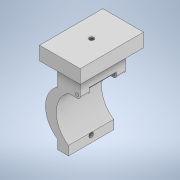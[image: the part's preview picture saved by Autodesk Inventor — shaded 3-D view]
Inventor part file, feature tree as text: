
AUTODESK INVENTOR PART (.ipt)
format: ipt  version: 2021 (Build 250183000, 183)  size: 187,904 bytes
history: native  units: in
note: dims shown in document units (in); Inventor stores cm internally (conversion verified against a paired STEP export)
features: sketch x6, extrude x5, hole x2, fillet x1
ambient origin geometry x8: Origin, YZ Plane, XZ Plane, XY Plane, X Axis, Y Axis, Z Axis, Center Point
bodies: Solid1 (feature_tree)
feature tree (14):
  extrude  "Extrusion1"  Depth=3.937in TaperAngle=0.0deg
  extrude  "Extrusion6"  Depth=1.9685in
  extrude  "Extrusion7"  Depth=0.7874in
  hole  "Hole3"  [1 undecoded]
  extrude  "Extrusion8"  Depth=1.9685in
  extrude  "Extrusion9"  Depth=0.7874in
  hole  "Hole4"  [1 undecoded]
  fillet  "Fillet1"  Radius=0.3937in
  sketch  "Sketch2"  dims[d1=1.9685in d2=3.937in d3=0.0in]
  sketch  "Sketch12"  dims[d56=3.937in d57=1.9685in]
  sketch  "Sketch13"  dims[d58=2.3622in d59=0.7874in]
  sketch  "Sketch16"  dims[d61=0.9449in d62=3.937in d63=0.0in]
  sketch  "Sketch18"  dims[d68=0.9843in d69=1.9685in]
  sketch  "Sketch19"  dims[d70=5.5118in d71=3.5433in d72=1.1811in d73=0.0in d74=0.3937in d75=0.315in d76=0.2362in d77=0.3937in d78=0.1181in d79=90.0deg d80=3.1496in d81=0.8108in d82=0.2756in d83=0.2756in d84=0.2756in d85=3.937in d86=0.0in d89=0.5118in d90=0.0in d91=0.5906in d92=0.3937in d93=0.3937in d94=0.2362in d95=0.3937in d96=0.1181in d97=90.0deg d98=0.315in d99=0.8108in d102=0.2362in d103=2.3622in d104=0.5512in d108=0.7874in d109=0.7874in d110=0.9449in d111=0.7874in d64=0.0197in d65=0.0344in d66=0.0197in d67=0.0344in]
note: 2 required parameter values undecoded (feature->parameter linkage not recoverable at this tier; creation-order binding heuristic only, values carry confidence <= 0.55)
